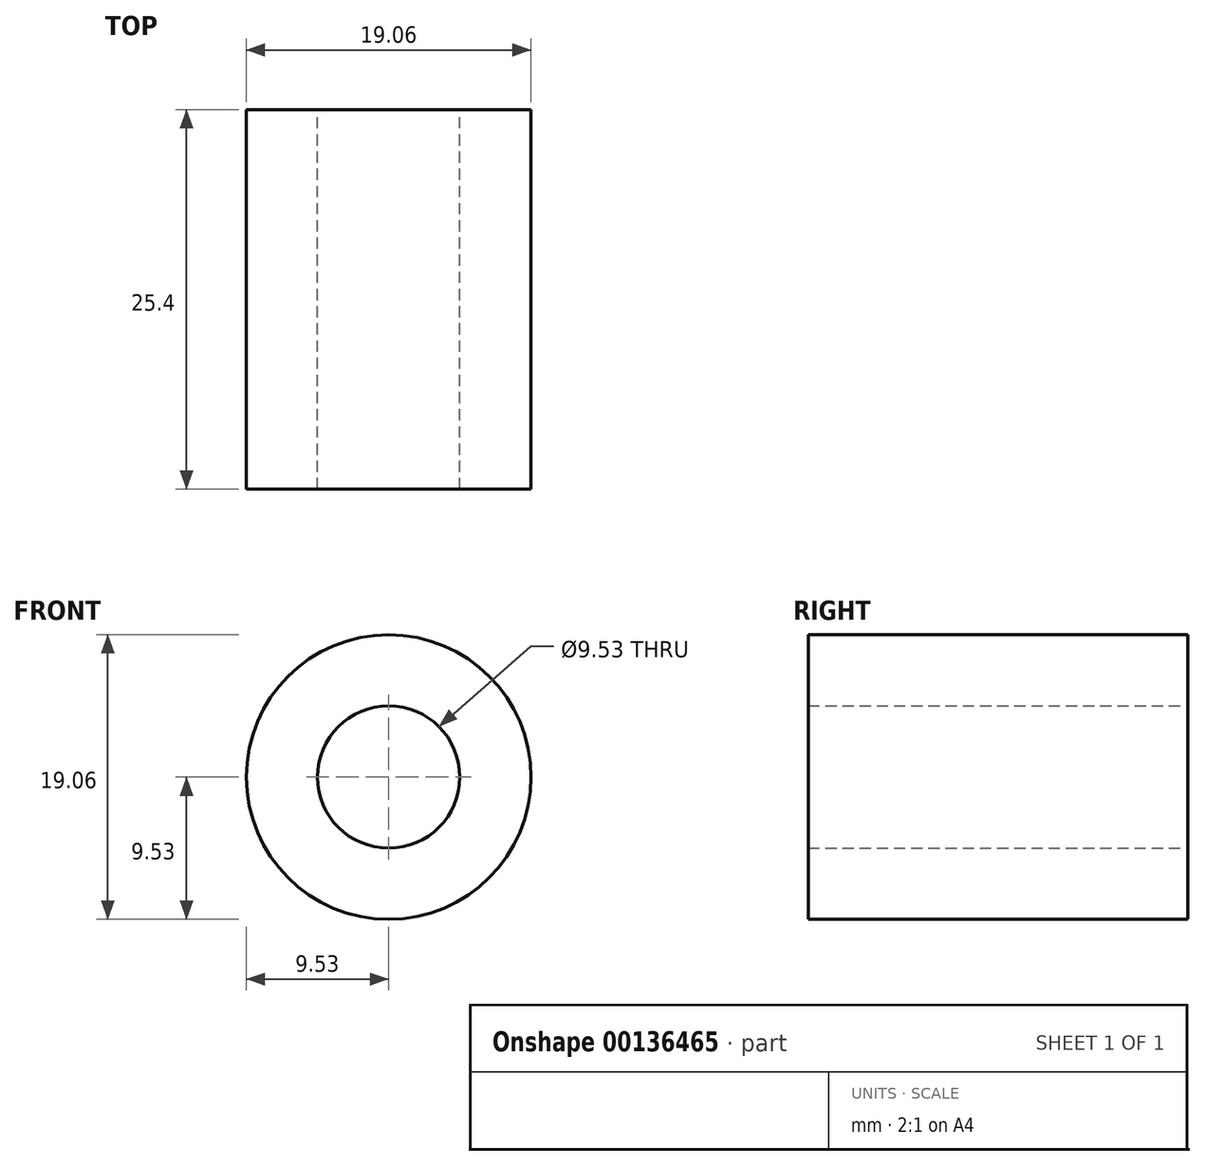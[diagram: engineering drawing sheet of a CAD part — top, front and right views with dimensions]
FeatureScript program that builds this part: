
annotation { "Feature Type Name" : "Feature", "Feature Type Description" : "" }
export const myFeature = defineFeature(function(context is Context, id is Id, definition is map)
    precondition{}
    {
        {
            var Q0;
            Q0=qCreatedBy(makeId("Front.planeOp"),FACE);
            var sketch = newSketch(context, id + "F0", { "sketchPlane" : qUnion([Q0])});
            skCircle(sketch, "E0", {"center": v(0, 0) * mm, "radius": 9.53 * mm});
            skSolve(sketch);
        }
        {
            var Q0;
            Q0=makeQuery(id+"F0.imprint","IMPRINT",FACE,{"disambiguationData":[TD([[makeQuery(id+"F0.imprint","IMPRINT",EDGE,{"derivedFrom":sQuery(id+"F0.wireOp",EDGE,"E0")}),1.0]])]});
            extrude(context, id + "F1", {"entities" : qUnion([Q0]), "depth" : 25.4 * mm});
        }
        {
            var Q0;
            Q0=makeQuery(id+"F1.opExtrude","CAP_FACE",FACE,{"disambiguationData":[OSD([sQuery(id+"F0.wireOp",EDGE,"E0")])],"isStart":true});
            var sketch = newSketch(context, id + "F2", { "sketchPlane" : qUnion([Q0])});
            skLineSegment(sketch, "E1.bottom", {"start": v(-4.76, 4.76) * mm, "end": v(4.76, 4.76) * mm});
            skLineSegment(sketch, "E1.top", {"start": v(-4.76, -4.76) * mm, "end": v(4.76, -4.76) * mm});
            skLineSegment(sketch, "E1.left", {"start": v(-4.76, 4.76) * mm, "end": v(-4.76, -4.76) * mm});
            skLineSegment(sketch, "E1.right", {"start": v(4.76, 4.76) * mm, "end": v(4.76, -4.76) * mm});
            skPoint(sketch, "E1.middle", {"position": v(0, 0) * mm});
            skCircle(sketch, "E2", {"center": v(0, 0) * mm, "radius": 4.76 * mm});
            skSolve(sketch);
        }
        {
            var Q0;
            {var subQ0=sQuery(id+"F2.wireOp",EDGE,"E2");var subQ1=makeQuery(id+"F2.imprint","INTERSECT",VERTEX,{"derivedFrom":[sQuery(id+"F2.wireOp",EDGE,"E1.bottom"),subQ0]});Q0=makeQuery(id+"F2.imprint","IMPRINT",FACE,{"disambiguationData":[TD([[makeQuery(id+"F2.imprint","IMPRINT",EDGE,{"disambiguationData":[TD([[subQ1,1.0]])],"derivedFrom":subQ0}),1.0]])]});}
            extrude(context, id + "F3", {"entities" : qUnion([Q0]), "operationType" : NewBodyOperationType.REMOVE, "endBound" : BoundingType.THROUGH_ALL, "oppositeDirection" : true, "depth" : 25.4 * mm});
        }
    });
